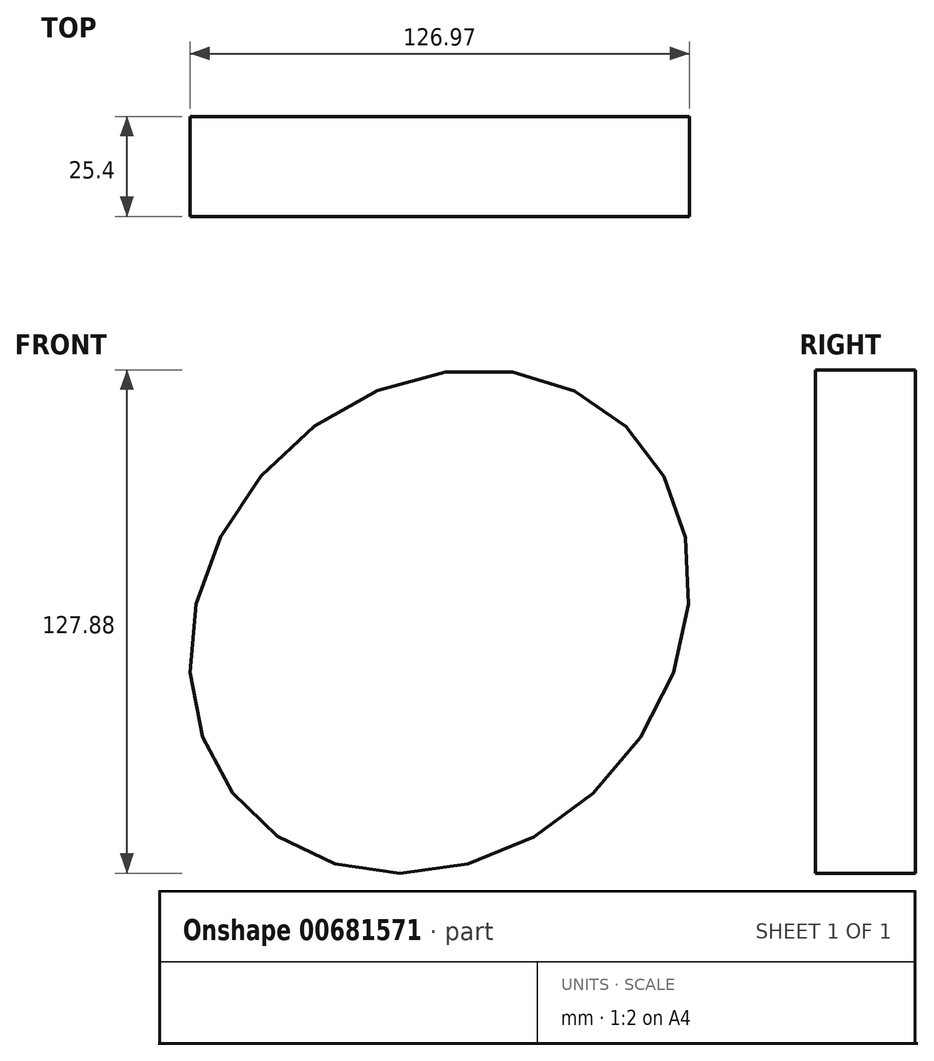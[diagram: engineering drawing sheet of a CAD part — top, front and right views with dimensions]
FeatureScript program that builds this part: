
annotation { "Feature Type Name" : "Feature", "Feature Type Description" : "" }
export const myFeature = defineFeature(function(context is Context, id is Id, definition is map)
    precondition{}
    {
        {
            var Q0;
            Q0=qCreatedBy(makeId("Front.planeOp"),FACE);
            var sketch = newSketch(context, id + "F0", { "sketchPlane" : qUnion([Q0])});
            skEllipse(sketch, "E0", {"center": v(76.16, 0) * mm, "majorRadius": 68.54 * mm, "minorRadius": 58.49 * mm, "majorAxis": v(0.7, 0.72)});
            skSolve(sketch);
        }
        {
            var Q0;
            Q0 = qSketchRegion(id + "F0", true);
            extrude(context, id + "F1", {"entities" : qUnion([Q0]), "depth" : 25.4 * mm, "offsetDistance" : 25.4 * mm});
        }
    });
